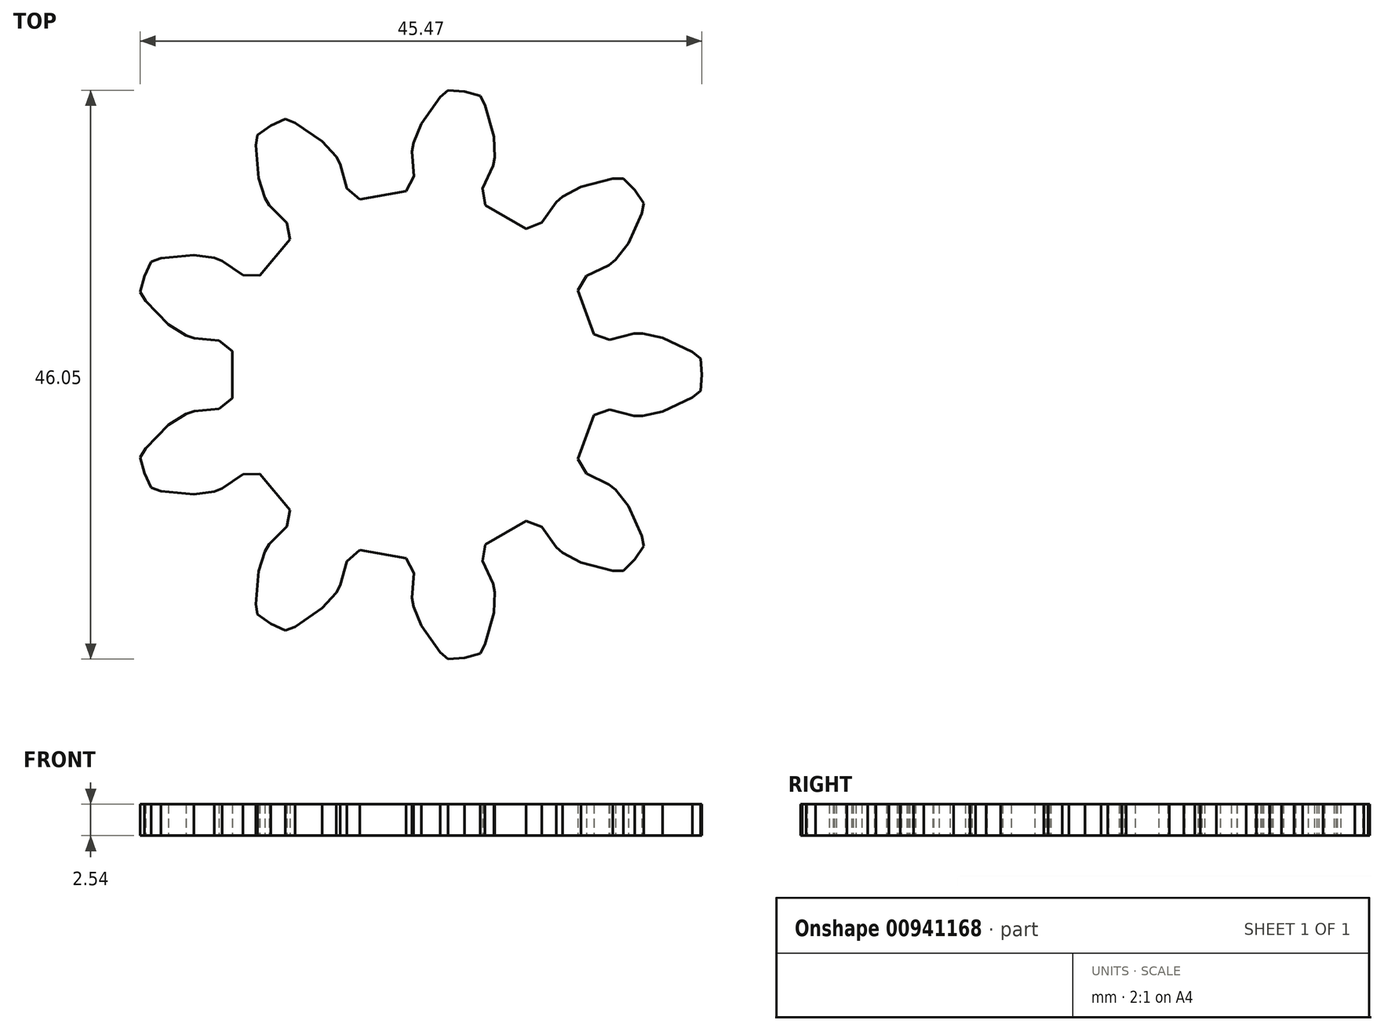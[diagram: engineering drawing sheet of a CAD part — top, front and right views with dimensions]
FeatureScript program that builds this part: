
annotation { "Feature Type Name" : "Feature", "Feature Type Description" : "" }
export const myFeature = defineFeature(function(context is Context, id is Id, definition is map)
    precondition{}
    {
        {
            var Q0;
            Q0=qCreatedBy(makeId("Top.planeOp"),FACE);
            var sketch = newSketch(context, id + "F0", { "sketchPlane" : qUnion([Q0])});
            skLineSegment(sketch, "E0", {"start": v(16.4, -15.98) * mm, "end": v(17.32, -15.05) * mm});
            skLineSegment(sketch, "E1", {"start": v(17.32, -15.05) * mm, "end": v(18.07, -13.98) * mm});
            skLineSegment(sketch, "E2", {"start": v(18.07, -13.98) * mm, "end": v(17.9, -13.15) * mm});
            skLineSegment(sketch, "E3", {"start": v(17.9, -13.15) * mm, "end": v(16.81, -10.73) * mm});
            skLineSegment(sketch, "E4", {"start": v(16.81, -10.73) * mm, "end": v(15.78, -9.4) * mm});
            skLineSegment(sketch, "E5", {"start": v(15.78, -9.4) * mm, "end": v(15.24, -8.97) * mm});
            skLineSegment(sketch, "E6", {"start": v(15.24, -8.97) * mm, "end": v(13.42, -8.1) * mm});
            skLineSegment(sketch, "E7", {"start": v(13.42, -8.1) * mm, "end": v(12.71, -6.93) * mm});
            skLineSegment(sketch, "E8", {"start": v(12.71, -6.93) * mm, "end": v(14.01, -3.36) * mm});
            skLineSegment(sketch, "E9", {"start": v(14.01, -3.36) * mm, "end": v(15.3, -2.91) * mm});
            skLineSegment(sketch, "E10", {"start": v(15.3, -2.91) * mm, "end": v(17.26, -3.42) * mm});
            skLineSegment(sketch, "E11", {"start": v(17.26, -3.42) * mm, "end": v(17.96, -3.43) * mm});
            skLineSegment(sketch, "E12", {"start": v(17.96, -3.43) * mm, "end": v(19.6, -3.08) * mm});
            skLineSegment(sketch, "E13", {"start": v(19.6, -3.08) * mm, "end": v(22, -1.93) * mm});
            skLineSegment(sketch, "E14", {"start": v(22, -1.93) * mm, "end": v(22.65, -1.4) * mm});
            skLineSegment(sketch, "E15", {"start": v(22.65, -1.4) * mm, "end": v(22.76, -0.1) * mm});
            skLineSegment(sketch, "E16", {"start": v(22.76, -0.1) * mm, "end": v(22.65, 1.21) * mm});
            skLineSegment(sketch, "E17", {"start": v(22.65, 1.21) * mm, "end": v(22, 1.74) * mm});
            skLineSegment(sketch, "E18", {"start": v(22, 1.74) * mm, "end": v(19.6, 2.89) * mm});
            skLineSegment(sketch, "E19", {"start": v(19.6, 2.89) * mm, "end": v(17.96, 3.24) * mm});
            skLineSegment(sketch, "E20", {"start": v(17.96, 3.24) * mm, "end": v(17.26, 3.23) * mm});
            skLineSegment(sketch, "E21", {"start": v(17.26, 3.23) * mm, "end": v(15.3, 2.72) * mm});
            skLineSegment(sketch, "E22", {"start": v(15.3, 2.72) * mm, "end": v(14.01, 3.16) * mm});
            skLineSegment(sketch, "E23", {"start": v(14.01, 3.16) * mm, "end": v(12.71, 6.74) * mm});
            skLineSegment(sketch, "E24", {"start": v(12.71, 6.74) * mm, "end": v(13.42, 7.9) * mm});
            skLineSegment(sketch, "E25", {"start": v(13.42, 7.9) * mm, "end": v(15.24, 8.78) * mm});
            skLineSegment(sketch, "E26", {"start": v(15.24, 8.78) * mm, "end": v(15.78, 9.21) * mm});
            skLineSegment(sketch, "E27", {"start": v(15.78, 9.21) * mm, "end": v(16.81, 10.54) * mm});
            skLineSegment(sketch, "E28", {"start": v(16.81, 10.54) * mm, "end": v(17.9, 12.96) * mm});
            skLineSegment(sketch, "E29", {"start": v(17.9, 12.96) * mm, "end": v(18.07, 13.78) * mm});
            skLineSegment(sketch, "E30", {"start": v(18.07, 13.78) * mm, "end": v(17.32, 14.86) * mm});
            skLineSegment(sketch, "E31", {"start": v(17.32, 14.86) * mm, "end": v(16.4, 15.79) * mm});
            skLineSegment(sketch, "E32", {"start": v(16.4, 15.79) * mm, "end": v(15.55, 15.77) * mm});
            skLineSegment(sketch, "E33", {"start": v(15.55, 15.77) * mm, "end": v(12.98, 15.1) * mm});
            skLineSegment(sketch, "E34", {"start": v(12.98, 15.1) * mm, "end": v(11.5, 14.33) * mm});
            skLineSegment(sketch, "E35", {"start": v(11.5, 14.33) * mm, "end": v(10.97, 13.87) * mm});
            skLineSegment(sketch, "E36", {"start": v(10.97, 13.87) * mm, "end": v(9.8, 12.22) * mm});
            skLineSegment(sketch, "E37", {"start": v(9.8, 12.22) * mm, "end": v(8.52, 11.73) * mm});
            skLineSegment(sketch, "E38", {"start": v(8.52, 11.73) * mm, "end": v(5.23, 13.63) * mm});
            skLineSegment(sketch, "E39", {"start": v(5.23, 13.63) * mm, "end": v(5.02, 14.98) * mm});
            skLineSegment(sketch, "E40", {"start": v(5.02, 14.98) * mm, "end": v(5.85, 16.82) * mm});
            skLineSegment(sketch, "E41", {"start": v(5.85, 16.82) * mm, "end": v(5.99, 17.5) * mm});
            skLineSegment(sketch, "E42", {"start": v(5.99, 17.5) * mm, "end": v(5.92, 19.18) * mm});
            skLineSegment(sketch, "E43", {"start": v(5.92, 19.18) * mm, "end": v(5.21, 21.74) * mm});
            skLineSegment(sketch, "E44", {"start": v(5.21, 21.74) * mm, "end": v(4.8, 22.48) * mm});
            skLineSegment(sketch, "E45", {"start": v(4.8, 22.48) * mm, "end": v(3.54, 22.82) * mm});
            skLineSegment(sketch, "E46", {"start": v(3.54, 22.82) * mm, "end": v(2.23, 22.93) * mm});
            skLineSegment(sketch, "E47", {"start": v(2.23, 22.93) * mm, "end": v(1.6, 22.38) * mm});
            skLineSegment(sketch, "E48", {"start": v(1.6, 22.38) * mm, "end": v(0.05, 20.22) * mm});
            skLineSegment(sketch, "E49", {"start": v(0.05, 20.22) * mm, "end": v(-0.59, 18.67) * mm});
            skLineSegment(sketch, "E50", {"start": v(-0.59, 18.67) * mm, "end": v(-0.7, 17.98) * mm});
            skLineSegment(sketch, "E51", {"start": v(-0.7, 17.98) * mm, "end": v(-0.54, 15.96) * mm});
            skLineSegment(sketch, "E52", {"start": v(-0.54, 15.96) * mm, "end": v(-1.2, 14.77) * mm});
            skLineSegment(sketch, "E53", {"start": v(-1.2, 14.77) * mm, "end": v(-4.94, 14.1) * mm});
            skLineSegment(sketch, "E54", {"start": v(-4.94, 14.1) * mm, "end": v(-5.97, 15) * mm});
            skLineSegment(sketch, "E55", {"start": v(-5.97, 15) * mm, "end": v(-6.5, 16.95) * mm});
            skLineSegment(sketch, "E56", {"start": v(-6.5, 16.95) * mm, "end": v(-6.85, 17.56) * mm});
            skLineSegment(sketch, "E57", {"start": v(-6.85, 17.56) * mm, "end": v(-7.97, 18.8) * mm});
            skLineSegment(sketch, "E58", {"start": v(-7.97, 18.8) * mm, "end": v(-10.16, 20.3) * mm});
            skLineSegment(sketch, "E59", {"start": v(-10.16, 20.3) * mm, "end": v(-10.95, 20.6) * mm});
            skLineSegment(sketch, "E60", {"start": v(-10.95, 20.6) * mm, "end": v(-12.14, 20.05) * mm});
            skLineSegment(sketch, "E61", {"start": v(-12.14, 20.05) * mm, "end": v(-13.21, 19.3) * mm});
            skLineSegment(sketch, "E62", {"start": v(-13.21, 19.3) * mm, "end": v(-13.34, 18.47) * mm});
            skLineSegment(sketch, "E63", {"start": v(-13.34, 18.47) * mm, "end": v(-13.14, 15.82) * mm});
            skLineSegment(sketch, "E64", {"start": v(-13.14, 15.82) * mm, "end": v(-12.63, 14.22) * mm});
            skLineSegment(sketch, "E65", {"start": v(-12.63, 14.22) * mm, "end": v(-12.27, 13.63) * mm});
            skLineSegment(sketch, "E66", {"start": v(-12.27, 13.63) * mm, "end": v(-10.85, 12.18) * mm});
            skLineSegment(sketch, "E67", {"start": v(-10.85, 12.18) * mm, "end": v(-10.59, 10.85) * mm});
            skLineSegment(sketch, "E68", {"start": v(-10.59, 10.85) * mm, "end": v(-13.03, 7.93) * mm});
            skLineSegment(sketch, "E69", {"start": v(-13.03, 7.93) * mm, "end": v(-14.4, 7.96) * mm});
            skLineSegment(sketch, "E70", {"start": v(-14.4, 7.96) * mm, "end": v(-16.06, 9.1) * mm});
            skLineSegment(sketch, "E71", {"start": v(-16.06, 9.1) * mm, "end": v(-16.71, 9.36) * mm});
            skLineSegment(sketch, "E72", {"start": v(-16.71, 9.36) * mm, "end": v(-18.37, 9.58) * mm});
            skLineSegment(sketch, "E73", {"start": v(-18.37, 9.58) * mm, "end": v(-21.01, 9.33) * mm});
            skLineSegment(sketch, "E74", {"start": v(-21.01, 9.33) * mm, "end": v(-21.81, 9.05) * mm});
            skLineSegment(sketch, "E75", {"start": v(-21.81, 9.05) * mm, "end": v(-22.37, 7.86) * mm});
            skLineSegment(sketch, "E76", {"start": v(-22.37, 7.86) * mm, "end": v(-22.7, 6.6) * mm});
            skLineSegment(sketch, "E77", {"start": v(-22.7, 6.6) * mm, "end": v(-22.27, 5.87) * mm});
            skLineSegment(sketch, "E78", {"start": v(-22.27, 5.87) * mm, "end": v(-20.41, 3.98) * mm});
            skLineSegment(sketch, "E79", {"start": v(-20.41, 3.98) * mm, "end": v(-19, 3.08) * mm});
            skLineSegment(sketch, "E80", {"start": v(-19, 3.08) * mm, "end": v(-18.34, 2.86) * mm});
            skLineSegment(sketch, "E81", {"start": v(-18.34, 2.86) * mm, "end": v(-16.32, 2.66) * mm});
            skLineSegment(sketch, "E82", {"start": v(-16.32, 2.66) * mm, "end": v(-15.26, 1.8) * mm});
            skLineSegment(sketch, "E83", {"start": v(-15.26, 1.8) * mm, "end": v(-15.26, -2) * mm});
            skLineSegment(sketch, "E84", {"start": v(-15.26, -2) * mm, "end": v(-16.32, -2.85) * mm});
            skLineSegment(sketch, "E85", {"start": v(-16.32, -2.85) * mm, "end": v(-18.34, -3.05) * mm});
            skLineSegment(sketch, "E86", {"start": v(-18.34, -3.05) * mm, "end": v(-19, -3.27) * mm});
            skLineSegment(sketch, "E87", {"start": v(-19, -3.27) * mm, "end": v(-20.41, -4.17) * mm});
            skLineSegment(sketch, "E88", {"start": v(-20.41, -4.17) * mm, "end": v(-22.27, -6.06) * mm});
            skLineSegment(sketch, "E89", {"start": v(-22.27, -6.06) * mm, "end": v(-22.7, -6.78) * mm});
            skLineSegment(sketch, "E90", {"start": v(-22.7, -6.78) * mm, "end": v(-22.37, -8.05) * mm});
            skLineSegment(sketch, "E91", {"start": v(-22.37, -8.05) * mm, "end": v(-21.81, -9.24) * mm});
            skLineSegment(sketch, "E92", {"start": v(-21.81, -9.24) * mm, "end": v(-21.01, -9.52) * mm});
            skLineSegment(sketch, "E93", {"start": v(-21.01, -9.52) * mm, "end": v(-18.37, -9.77) * mm});
            skLineSegment(sketch, "E94", {"start": v(-18.37, -9.77) * mm, "end": v(-16.71, -9.55) * mm});
            skLineSegment(sketch, "E95", {"start": v(-16.71, -9.55) * mm, "end": v(-16.06, -9.3) * mm});
            skLineSegment(sketch, "E96", {"start": v(-16.06, -9.3) * mm, "end": v(-14.4, -8.15) * mm});
            skLineSegment(sketch, "E97", {"start": v(-14.4, -8.15) * mm, "end": v(-13.03, -8.12) * mm});
            skLineSegment(sketch, "E98", {"start": v(-13.03, -8.12) * mm, "end": v(-10.59, -11.04) * mm});
            skLineSegment(sketch, "E99", {"start": v(-10.59, -11.04) * mm, "end": v(-10.85, -12.38) * mm});
            skLineSegment(sketch, "E100", {"start": v(-10.85, -12.38) * mm, "end": v(-12.27, -13.82) * mm});
            skLineSegment(sketch, "E101", {"start": v(-12.27, -13.82) * mm, "end": v(-12.63, -14.42) * mm});
            skLineSegment(sketch, "E102", {"start": v(-12.63, -14.42) * mm, "end": v(-13.14, -16.01) * mm});
            skLineSegment(sketch, "E103", {"start": v(-13.14, -16.01) * mm, "end": v(-13.34, -18.66) * mm});
            skLineSegment(sketch, "E104", {"start": v(-13.34, -18.66) * mm, "end": v(-13.21, -19.5) * mm});
            skLineSegment(sketch, "E105", {"start": v(-13.21, -19.5) * mm, "end": v(-12.14, -20.25) * mm});
            skLineSegment(sketch, "E106", {"start": v(-12.14, -20.25) * mm, "end": v(-10.95, -20.8) * mm});
            skLineSegment(sketch, "E107", {"start": v(-10.95, -20.8) * mm, "end": v(-10.16, -20.5) * mm});
            skLineSegment(sketch, "E108", {"start": v(-10.16, -20.5) * mm, "end": v(-7.97, -19) * mm});
            skLineSegment(sketch, "E109", {"start": v(-7.97, -19) * mm, "end": v(-6.85, -17.75) * mm});
            skLineSegment(sketch, "E110", {"start": v(-6.85, -17.75) * mm, "end": v(-6.5, -17.14) * mm});
            skLineSegment(sketch, "E111", {"start": v(-6.5, -17.14) * mm, "end": v(-5.97, -15.2) * mm});
            skLineSegment(sketch, "E112", {"start": v(-5.97, -15.2) * mm, "end": v(-4.94, -14.3) * mm});
            skLineSegment(sketch, "E113", {"start": v(-4.94, -14.3) * mm, "end": v(-1.2, -14.96) * mm});
            skLineSegment(sketch, "E114", {"start": v(-1.2, -14.96) * mm, "end": v(-0.54, -16.15) * mm});
            skLineSegment(sketch, "E115", {"start": v(-0.54, -16.15) * mm, "end": v(-0.7, -18.17) * mm});
            skLineSegment(sketch, "E116", {"start": v(-0.7, -18.17) * mm, "end": v(-0.59, -18.86) * mm});
            skLineSegment(sketch, "E117", {"start": v(-0.59, -18.86) * mm, "end": v(0.05, -20.4) * mm});
            skLineSegment(sketch, "E118", {"start": v(0.05, -20.4) * mm, "end": v(1.6, -22.57) * mm});
            skLineSegment(sketch, "E119", {"start": v(1.6, -22.57) * mm, "end": v(2.23, -23.12) * mm});
            skLineSegment(sketch, "E120", {"start": v(2.23, -23.12) * mm, "end": v(3.54, -23) * mm});
            skLineSegment(sketch, "E121", {"start": v(3.54, -23) * mm, "end": v(4.8, -22.67) * mm});
            skLineSegment(sketch, "E122", {"start": v(4.8, -22.67) * mm, "end": v(5.21, -21.93) * mm});
            skLineSegment(sketch, "E123", {"start": v(5.21, -21.93) * mm, "end": v(5.92, -19.37) * mm});
            skLineSegment(sketch, "E124", {"start": v(5.92, -19.37) * mm, "end": v(5.99, -17.7) * mm});
            skLineSegment(sketch, "E125", {"start": v(5.99, -17.7) * mm, "end": v(5.85, -17.01) * mm});
            skLineSegment(sketch, "E126", {"start": v(5.85, -17.01) * mm, "end": v(5.02, -15.17) * mm});
            skLineSegment(sketch, "E127", {"start": v(5.02, -15.17) * mm, "end": v(5.23, -13.83) * mm});
            skLineSegment(sketch, "E128", {"start": v(5.23, -13.83) * mm, "end": v(8.52, -11.92) * mm});
            skLineSegment(sketch, "E129", {"start": v(8.52, -11.92) * mm, "end": v(9.8, -12.42) * mm});
            skLineSegment(sketch, "E130", {"start": v(9.8, -12.42) * mm, "end": v(10.97, -14.06) * mm});
            skLineSegment(sketch, "E131", {"start": v(10.97, -14.06) * mm, "end": v(11.5, -14.52) * mm});
            skLineSegment(sketch, "E132", {"start": v(11.5, -14.52) * mm, "end": v(12.98, -15.3) * mm});
            skLineSegment(sketch, "E133", {"start": v(12.98, -15.3) * mm, "end": v(15.55, -15.96) * mm});
            skLineSegment(sketch, "E134", {"start": v(15.55, -15.96) * mm, "end": v(16.4, -15.98) * mm});
            skSolve(sketch);
        }
        {
            var Q0;
            Q0 = qSketchRegion(id + "F0", true);
            extrude(context, id + "F1", {"entities" : qUnion([Q0]), "depth" : 2.54 * mm, "offsetDistance" : 25.4 * mm});
        }
    });
